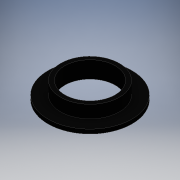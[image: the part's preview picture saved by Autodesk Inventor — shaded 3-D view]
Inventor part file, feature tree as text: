
AUTODESK INVENTOR PART (.ipt)
format: ipt  version: 2016 (Build 200138000, 138)  size: 103,936 bytes
history: native  units: mm
features: extrude x2, other x1, sketch x1
ambient origin geometry x8: Origin, YZ Plane, XZ Plane, XY Plane, X Axis, Y Axis, Z Axis, Center Point
bodies: Body1 (feature_tree)
feature tree (4):
  other  "ソリッド1"
  sketch  "スケッチ1"
  extrude  "押し出し1"  Depth=14.0mm
  extrude  "押し出し2"  Depth=12.0mm
